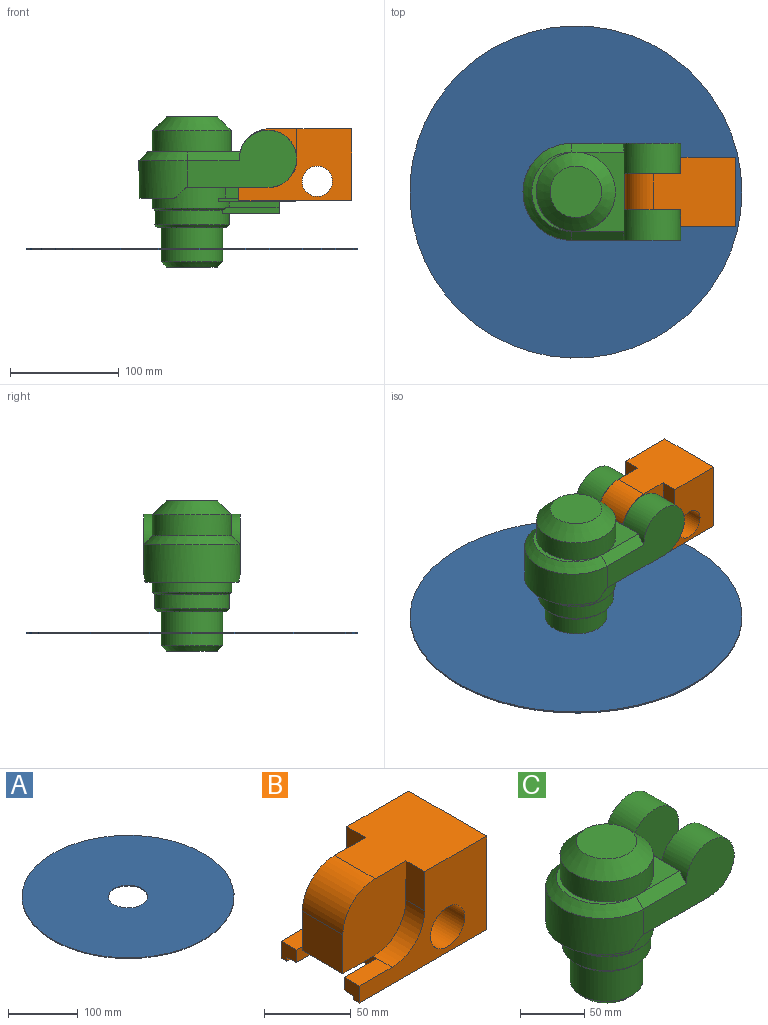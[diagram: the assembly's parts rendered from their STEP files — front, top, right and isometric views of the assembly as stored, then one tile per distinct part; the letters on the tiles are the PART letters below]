
ASSEMBLY  parts=3 mates=4
PART A: 4 faces, bbox 304.8x304.8x1.3 mm
  f0: cylinder r=28.26mm len=56.52mm, axis (0,0,-1), area 225.5mm2, adj f2,f3
  f1: cylinder r=152.4mm len=304.8mm, axis (0,0,-1), area 1216.1mm2, adj f2,f3
  f2: plane 304.8x304.8mm, normal (0,0,1), area 70457.4mm2, adj f0,f1
  f3: plane 304.8x304.8mm, normal (0,0,-1), area 70457.4mm2, adj f0,f1
PART B: 27 faces, bbox 103.7x63.5x66 mm
  f0: plane 26.67x8.88mm, normal (0,-1,0), area 236.7mm2, adj f1,f5,f19,f23
  f1: plane 38.61x9.13mm, normal (-1,0,0), area 325.8mm2, adj f0,f3,f7,f8,f13,f18,f21,f23
  f2: plane 12.45x11.87mm, normal (-1,0,0), area 126.1mm2, adj f3,f9,f10,f22,f25,f26
  f3: plane 26.67x8.88mm, normal (0,1,0), area 236.7mm2, adj f1,f2,f22,f26
  f4: plane 75.61x63.5mm, normal (0,0,1), area 4034.9mm2, adj f6,f7,f8,f10,f11,f15,f17,f20
  f5: plane 12.45x11.87mm, normal (-1,0,0), area 126.1mm2, adj f0,f6,f9,f19,f23,f24
  f6: plane 103.68x66.04mm, normal (0,1,0), area 3502.7mm2, adj f4,f5,f9,f11,f16,f17,f18,f19
  f7: plane 54.17x51.44mm, normal (0,-1,0), area 2480.2mm2, adj f1,f4,f13,f14,f15,f20,f21
  f8: plane 54.17x51.44mm, normal (0,1,0), area 2480.2mm2, adj f1,f4,f13,f14,f15,f17,f18
  f9: plane 103.68x63.5mm, normal (0,0,-1), area 3746.7mm2, adj f2,f5,f6,f10,f11,f12,f24,f25
  f10: plane 103.68x66.04mm, normal (0,-1,0), area 3502.7mm2, adj f2,f4,f9,f11,f16,f20,f21,f22
  f11: plane 66.04x63.5mm, normal (1,0,0), area 4193.5mm2, adj f4,f6,f9,f10
  f12: plane 54.48x4.31mm, normal (-1,0,0), area 184.3mm2, adj f9,f23,f24,f25,f26
  f13: plane 33.02x24.89mm, normal (0,0,-1), area 821.9mm2, adj f1,f7,f8,f14
  f14: plane 33.02x27.62mm, normal (-1,0,0), area 912.1mm2, adj f7,f8,f13,f15
  f15: cylinder r=26.29mm len=33.02mm, axis (0,-1,0), area 1363.5mm2, adj f4,f7,f8,f14
  f16: cylinder r=13.97mm len=63.5mm, axis (0,-1,0), area 5573.8mm2, adj f6,f10
  f17: plane 27.62x15.24mm, normal (-1,0,0), area 421mm2, adj f4,f6,f8,f18
  f18: cylinder r=26.54mm len=26.54mm, axis (0,1,0), area 635.4mm2, adj f1,f6,f8,f17,f19
  f19: plane 26.67x12.45mm, normal (0,0,1), area 331.9mm2, adj f0,f5,f6,f18
  f20: plane 27.62x15.24mm, normal (-1,0,0), area 421mm2, adj f4,f7,f10,f21
  f21: cylinder r=26.54mm len=26.54mm, axis (0,-1,0), area 635.4mm2, adj f1,f7,f10,f20,f22
  f22: plane 26.67x12.45mm, normal (0,0,1), area 331.9mm2, adj f2,f3,f10,f21
  f23: plane 52.07x27.24mm, normal (0,-0.07,-1), area 905.7mm2, adj f0,f1,f5,f12,f24,f26
  f24: plane 52.07x2.46mm, normal (0,-1,0), area 128.1mm2, adj f5,f9,f12,f23
  f25: plane 52.07x2.46mm, normal (0,1,0), area 128.1mm2, adj f2,f9,f12,f26
  f26: plane 52.07x27.24mm, normal (0,0.07,-1), area 905.7mm2, adj f1,f2,f3,f12,f23,f25
PART C: 52 faces, bbox 144.8x89x137.9 mm
  f0: cylinder r=34.29mm len=68.58mm, axis (0,0,-1), area 2720.2mm2, adj f2,f6,f21,f22,f24
  f1: cylinder r=36.32mm len=72.64mm, axis (0,0,-1), area 2698.7mm2, adj f2,f8,f9,f11,f12,f13,f14,f15
  f2: cone r=36.32mm half-angle=45deg, axis (0,0,1), area 519.6mm2, adj f0,f1,f21,f22
  f3: cylinder r=28.26mm len=56.52mm, axis (0,0,-1), area 5524.4mm2, adj f5,f7
  f4: plane 46.36x46.36mm, normal (0,0,-1), area 1687.7mm2, adj f7
  f5: plane 63.5x63.5mm, normal (0,0,-1), area 658.4mm2, adj f3,f6
  f6: cone r=34.29mm half-angle=45deg, axis (0,0,1), area 745.3mm2, adj f0,f5
  f7: cone r=28.26mm half-angle=45deg, axis (0,0,1), area 1160.9mm2, adj f3,f4
  f8: plane 39.08x9.39mm, normal (0,1,0), area 366.8mm2, adj f1,f9,f23,f46
  f9: plane 73.33x25.15mm, normal (0,0,-1), area 1415.4mm2, adj f1,f8,f16,f31,f33
  f10: plane 72.64x44.34mm, normal (0,0,1), area 1148.7mm2, adj f31,f38,f40,f51
  f11: plane 45.49x5.27mm, normal (0,-1,0), area 239.8mm2, adj f1,f25,f26,f28
  f12: plane 45.49x5.84mm, normal (0,1,0), area 265.8mm2, adj f1,f25,f27,f28
  f13: plane 10.94x7.04mm, normal (0.71,0,-0.71), area 90.5mm2, adj f1,f15,f16,f36
  f14: cylinder r=5.08mm len=11.55mm, axis (0,-1,0), area 40.5mm2, adj f1,f35,f36,f37
  f15: cylinder r=5.08mm len=11.55mm, axis (0,-1,0), area 40.5mm2, adj f1,f13,f35,f36
  f16: cylinder r=5.08mm len=8.82mm, axis (0,1,0), area 34mm2, adj f1,f9,f13,f33,f36
  f17: cylinder r=5.08mm len=8.82mm, axis (0,1,0), area 34mm2, adj f1,f30,f32,f36,f37
  f18: plane 70.94x3.18mm, normal (0,1,0), area 225.2mm2, adj f1,f28,f29,f46
  f19: plane 70.94x3.18mm, normal (0,-1,0), area 225.2mm2, adj f1,f28,f29,f45,f48
  f20: plane 39.08x9.91mm, normal (0,-1,0), area 387.2mm2, adj f1,f23,f32,f47,f48
  f21: plane 51.76x5.31mm, normal (0,1,0), area 269.6mm2, adj f0,f1,f2,f24,f25,f27
  f22: plane 51.76x5.89mm, normal (0,-1,0), area 297.8mm2, adj f0,f1,f2,f24,f25,f26
  f23: plane 38.61x9.39mm, normal (1,0,0), area 337.1mm2, adj f8,f20,f31,f42,f45,f46
  f24: plane 51.71x38.74mm, normal (0,0,-1), area 1845.4mm2, adj f0,f21,f22,f25
  f25: plane 38.74x11.11mm, normal (1,0,0), area 340.8mm2, adj f11,f12,f21,f22,f24,f26,f27,f28
  f26: plane 49.28x8.06mm, normal (0,0,1), area 380.5mm2, adj f1,f11,f22,f25
  f27: plane 49.28x8.06mm, normal (0,0,1), area 380.5mm2, adj f1,f12,f21,f25
  f28: plane 70.94x53.98mm, normal (0,0,-1), area 2379mm2, adj f1,f11,f12,f18,f19,f25,f29
  f29: plane 53.98x5mm, normal (1,0,0), area 220.7mm2, adj f18,f19,f28,f45,f46
  f30: plane 100.2x52.61mm, normal (0,-1,0), area 3486.8mm2, adj f17,f31,f32,f36,f38
  f31: cylinder r=26.29mm len=88.9mm, axis (0,-1,0), area 6645.5mm2, adj f9,f10,f23,f30,f32,f33,f38,f40
  f32: plane 73.33x25.15mm, normal (0,0,-1), area 1415.4mm2, adj f1,f17,f20,f30,f31
  f33: plane 100.2x52.61mm, normal (0,1,0), area 3486.8mm2, adj f9,f16,f31,f36,f40
  f34: plane 72.64x40.39mm, normal (0,0,1), area 295.2mm2, adj f38,f39,f40,f51
  f35: plane 84.68x30.92mm, normal (0,0,-1), area 1073.4mm2, adj f1,f14,f15,f36
  f36: cylinder r=44.45mm len=88.9mm, axis (0,0,1), area 4676.8mm2, adj f13,f14,f15,f16,f17,f30,f33,f35
  f37: plane 10.94x7.04mm, normal (0.71,0,-0.71), area 90.5mm2, adj f1,f14,f17,f36
  f38: plane 48.46x8.19mm, normal (0,-0.71,0.71), area 549.8mm2, adj f10,f30,f31,f34,f39
  f39: cone r=36.32mm half-angle=45deg, axis (0,0,-1), area 1458.4mm2, adj f34,f36,f38,f40
  f40: plane 48.46x8.19mm, normal (0,0.71,0.71), area 549.8mm2, adj f10,f31,f33,f34,f39
  f41: plane 52.58x51.69mm, normal (0,1,0), area 2292.1mm2, adj f31,f42,f44
  f42: plane 33.02x25.4mm, normal (0,0,1), area 838.7mm2, adj f23,f41,f43,f44
  f43: plane 52.58x51.69mm, normal (0,-1,0), area 2292.1mm2, adj f31,f42,f44
  f44: plane 33.07x33.02mm, normal (1,0,0), area 1091.9mm2, adj f31,f41,f42,f43
  f45: plane 26.99x25.4mm, normal (0,-0.07,1), area 687.1mm2, adj f19,f23,f29,f46,f47
  f46: plane 70.97x27.02mm, normal (0,0.07,1), area 1010.6mm2, adj f1,f8,f18,f23,f29,f45
  f47: plane 7.68x0.52mm, normal (-1,0,0), area 2mm2, adj f20,f45,f48
  f48: plane 45.54x7.68mm, normal (0,0,1), area 322.8mm2, adj f1,f19,f20,f47
  f49: plane 47.24x47.24mm, normal (0,0,1), area 1753mm2, adj f50
  f50: cone r=23.62mm half-angle=45deg, axis (0,0,-1), area 3382.3mm2, adj f49,f51
  f51: cylinder r=36.32mm len=72.64mm, axis (0,0,-1), area 4420mm2, adj f10,f34,f50
PLACE A t=(290.68,602.24,175.89)mm
PLACE B t=(290.68,602.24,160.01)mm
PLACE C t=(290.68,602.24,160.01)mm
MATE planar C.f31 <-> B.f7  axis (0,1,0) through (360.53,585.73,259.39)mm
MATE planar B.f12 <-> C.f29  axis (-1,0,0) through (385.93,602.24,222.71)mm
MATE planar C.f3 <-> A.f1  axis (0,0,-1) through (290.68,602.24,160.01)mm
MATE cylindrical C.f3 <-> A.f0  axis (0,0,-1) through (290.68,602.24,180.65)mm
